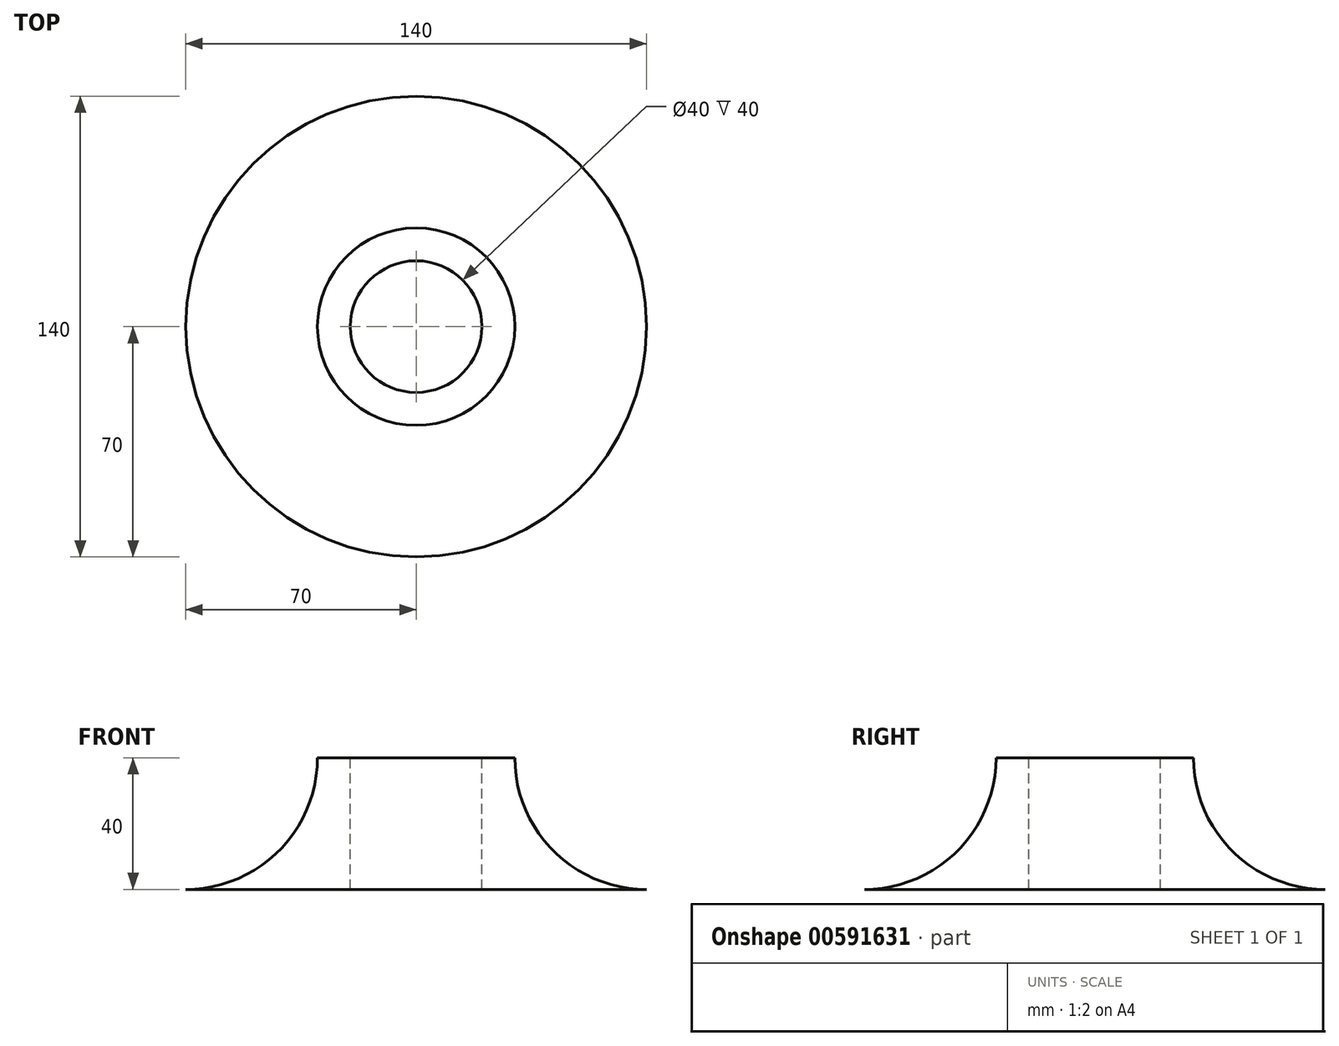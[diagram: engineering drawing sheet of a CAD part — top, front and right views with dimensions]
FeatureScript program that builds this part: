
annotation { "Feature Type Name" : "Feature", "Feature Type Description" : "" }
export const myFeature = defineFeature(function(context is Context, id is Id, definition is map)
    precondition{}
    {
        {
            var Q0;
            Q0=qCreatedBy(makeId("Front.planeOp"),FACE);
            var sketch = newSketch(context, id + "F0", { "sketchPlane" : qUnion([Q0])});
            skLineSegment(sketch, "E0", {"start": v(57.6, 40) * mm, "end": v(67.6, 40) * mm});
            skLineSegment(sketch, "E1", {"start": v(67.6, 40) * mm, "end": v(67.6, 0) * mm});
            skLineSegment(sketch, "E2", {"start": v(67.6, 0) * mm, "end": v(17.6, 0) * mm});
            skArc(sketch, "E3", {"start": v(17.6, 0) * mm, "mid": v(45.87, 11.72) * mm, "end": v(57.6, 40) * mm});
            skLineSegment(sketch, "E4", {"start": v(87.6, 56.81) * mm, "end": v(87.6, -13.7) * mm, "construction": true});
            skSolve(sketch);
        }
        {
            var Q0;
            Q0=makeQuery(id+"F0.imprint","IMPRINT",FACE,{"disambiguationData":[TD([[makeQuery(id+"F0.imprint","IMPRINT",EDGE,{"derivedFrom":sQuery(id+"F0.wireOp",EDGE,"E0")}),-1.0]])]});
            var Q1;
            Q1=sQuery(id+"F0.wireOp",EDGE,"E4");
            revolve(context, id + "F1", {"entities" : qUnion([Q0]), "axis" : qUnion([Q1]), "revolveType" : RevolveType.FULL});
        }
    });
